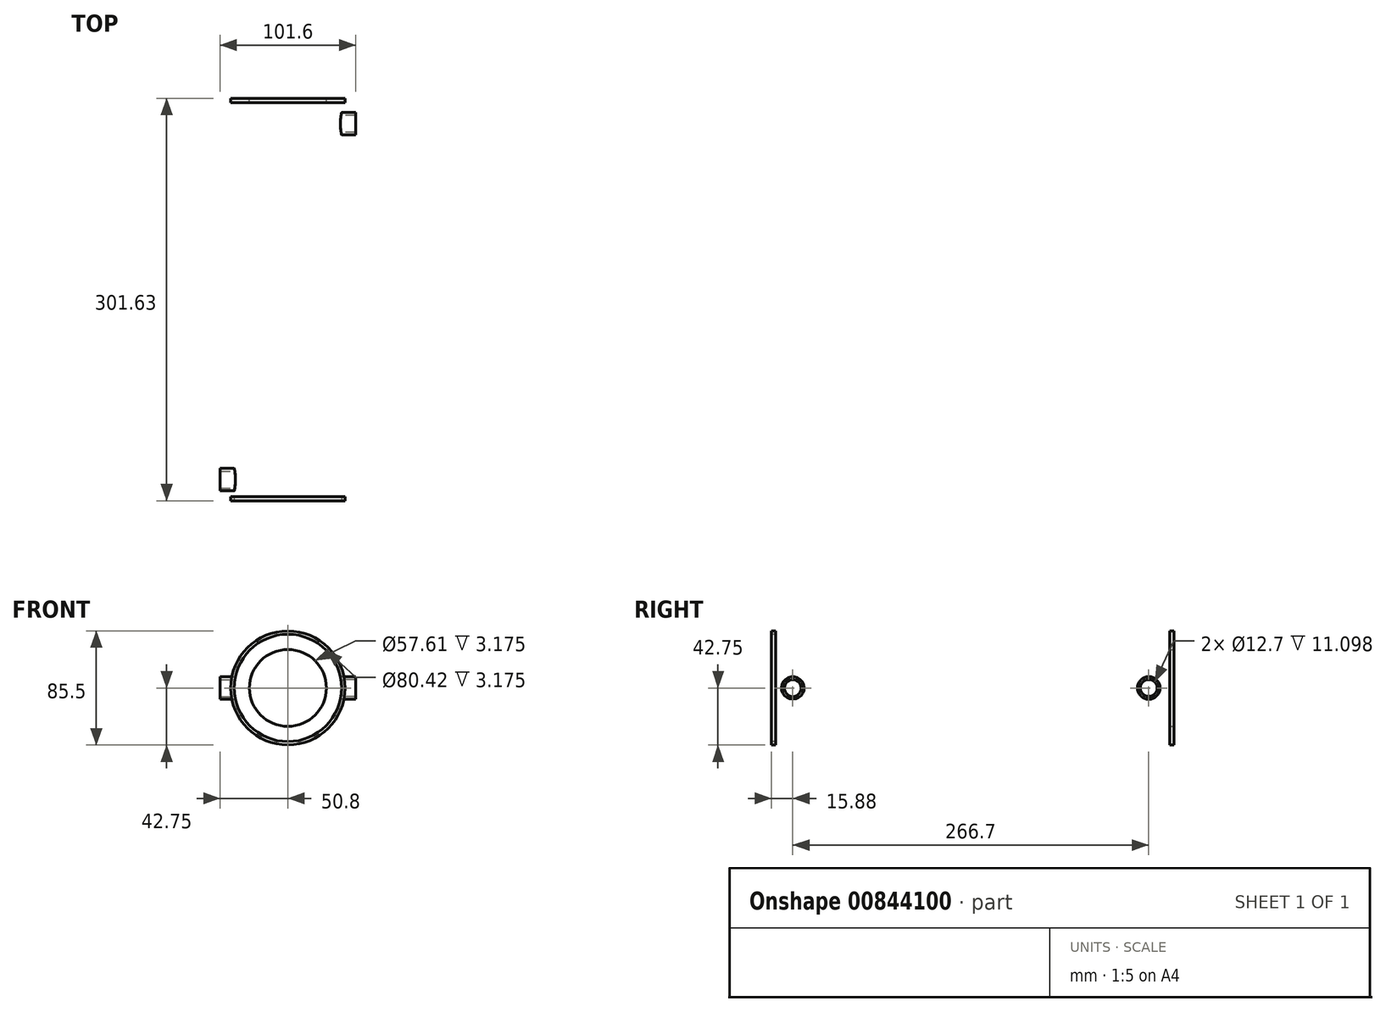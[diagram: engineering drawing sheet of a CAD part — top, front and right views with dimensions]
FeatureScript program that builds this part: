
annotation { "Feature Type Name" : "Feature", "Feature Type Description" : "" }
export const myFeature = defineFeature(function(context is Context, id is Id, definition is map)
    precondition{}
    {
        {
            var Q0;
            Q0=qCreatedBy(makeId("Front.planeOp"),FACE);
            var sketch = newSketch(context, id + "F0", { "sketchPlane" : qUnion([Q0])});
            skCircle(sketch, "E0", {"center": v(0, 0) * mm, "radius": 40.2 * mm});
            skCircle(sketch, "E1", {"center": v(0, 0) * mm, "radius": 42.75 * mm});
            skCircle(sketch, "E2", {"center": v(0, 0) * mm, "radius": 38.1 * mm});
            skCircle(sketch, "E3", {"center": v(0, 0) * mm, "radius": 28.8 * mm});
            skSolve(sketch);
        }
        {
            var Q0;
            Q0=makeQuery(id+"F0.imprint","IMPRINT",FACE,{"disambiguationData":[TD([[makeQuery(id+"F0.imprint","IMPRINT",EDGE,{"derivedFrom":sQuery(id+"F0.wireOp",EDGE,"E0")}),1.0]])]});
            extrude(context, id + "F1", {"entities" : qUnion([Q0]), "depth" : 301.62 * mm, "offsetDistance" : 25.4 * mm});
        }
        {
            var Q0;
            Q0 = qSketchRegion(id + "F0", true);
            var Q1;
            Q1=makeQuery(id+"F0.imprint","IMPRINT",FACE,{"disambiguationData":[TD([[makeQuery(id+"F0.imprint","IMPRINT",EDGE,{"derivedFrom":sQuery(id+"F0.wireOp",EDGE,"E2")}),1.0]])]});
            extrude(context, id + "F2", {"entities" : qUnion([Q0, Q1]), "operationType" : NewBodyOperationType.ADD, "depth" : 3.17 * mm, "offsetDistance" : 25.4 * mm});
        }
        {
            var Q0;
            Q0=qCreatedBy(makeId("Front.planeOp"),FACE);
            cPlane(context, id + "F3", {"entities" : qUnion([Q0]), "cplaneType" : CPlaneType.OFFSET, "offset" : 301.62 * mm, "width" : 152.4 * mm, "height" : 152.4 * mm});
        }
        {
            var Q0;
            Q0=qCreatedBy(id+"F3.planeOp",FACE);
            var sketch = newSketch(context, id + "F4", { "sketchPlane" : qUnion([Q0])});
            skCircle(sketch, "E4", {"center": v(0, 0) * mm, "radius": 42.75 * mm});
            skCircle(sketch, "E5", {"center": v(0, 0) * mm, "radius": 40.2 * mm});
            skCircle(sketch, "E6", {"center": v(0, 0) * mm, "radius": 28.8 * mm});
            skSolve(sketch);
        }
        {
            var Q0;
            Q0=makeQuery(id+"F4.imprint","IMPRINT",FACE,{"disambiguationData":[TD([[makeQuery(id+"F4.imprint","IMPRINT",EDGE,{"derivedFrom":sQuery(id+"F4.wireOp",EDGE,"E5")}),1.0]])]});
            var Q1;
            Q1=makeQuery(id+"F4.imprint","IMPRINT",FACE,{"disambiguationData":[TD([[makeQuery(id+"F4.imprint","IMPRINT",EDGE,{"derivedFrom":sQuery(id+"F4.wireOp",EDGE,"E4")}),1.0]])]});
            extrude(context, id + "F5", {"entities" : qUnion([Q0, Q1]), "operationType" : NewBodyOperationType.ADD, "oppositeDirection" : true, "depth" : 3.17 * mm, "offsetDistance" : 25.4 * mm});
        }
        {
            var Q0;
            Q0=qCreatedBy(makeId("Right.planeOp"),FACE);
            var sketch = newSketch(context, id + "F6", { "sketchPlane" : qUnion([Q0])});
            skCircle(sketch, "E7", {"center": v(-285.75, 0) * mm, "radius": 8.46 * mm});
            skCircle(sketch, "E8", {"center": v(-19.05, 0) * mm, "radius": 8.46 * mm});
            skCircle(sketch, "E9", {"center": v(-19.05, 0) * mm, "radius": 6.35 * mm});
            skCircle(sketch, "E10", {"center": v(-285.75, 0) * mm, "radius": 6.35 * mm});
            skSolve(sketch);
        }
        {
            var Q0;
            Q0=makeQuery(id+"F6.imprint","IMPRINT",FACE,{"disambiguationData":[TD([[makeQuery(id+"F6.imprint","IMPRINT",EDGE,{"derivedFrom":sQuery(id+"F6.wireOp",EDGE,"E8")}),1.0]])]});
            extrude(context, id + "F7", {"entities" : qUnion([Q0]), "depth" : 50.8 * mm, "offsetDistance" : 25.4 * mm});
        }
        {
            var Q0;
            Q0=makeQuery(id+"F6.imprint","IMPRINT",FACE,{"disambiguationData":[TD([[makeQuery(id+"F6.imprint","IMPRINT",EDGE,{"derivedFrom":sQuery(id+"F6.wireOp",EDGE,"E7")}),1.0]])]});
            extrude(context, id + "F8", {"entities" : qUnion([Q0]), "oppositeDirection" : true, "depth" : 50.8 * mm, "offsetDistance" : 25.4 * mm});
        }
        {
            var Q0;
            Q0=sQuery(id+"F6.wireOp",VERTEX,"E8.center");
            var Q1;
            Q1=makeQuery(id+"F1.opExtrude","SWEPT_BODY",BODY,{"disambiguationData":[OSD([sQuery(id+"F0.wireOp",EDGE,"E0"),sQuery(id+"F0.wireOp",EDGE,"E2")])]});
            hole(context, id + "F9", {"style" : HoleStyle.SIMPLE, "endStyle" : HoleEndStyle.THROUGH, "oppositeDirection" : true, "holeDiameter" : 12.7 * mm, "majorDiameter" : 6.35 * mm, "isTappedThrough" : true, "tappedDepth" : 12.7 * mm, "tapClearance" : 3, "locations" : qUnion([Q0]), "scope" : qUnion([Q1])});
        }
        {
            var Q0;
            Q0=sQuery(id+"F6.wireOp",VERTEX,"E7.center");
            var Q1;
            Q1=makeQuery(id+"F1.opExtrude","SWEPT_BODY",BODY,{"disambiguationData":[OSD([sQuery(id+"F0.wireOp",EDGE,"E0"),sQuery(id+"F0.wireOp",EDGE,"E2")])]});
            hole(context, id + "F10", {"style" : HoleStyle.SIMPLE, "endStyle" : HoleEndStyle.THROUGH, "holeDiameter" : 12.7 * mm, "majorDiameter" : 6.35 * mm, "isTappedThrough" : true, "tappedDepth" : 12.7 * mm, "tapClearance" : 3, "locations" : qUnion([Q0]), "scope" : qUnion([Q1])});
        }
        {
            var Q0;
            Q0=makeQuery(id+"F4.imprint","IMPRINT",FACE,{"disambiguationData":[TD([[makeQuery(id+"F4.imprint","IMPRINT",EDGE,{"derivedFrom":sQuery(id+"F4.wireOp",EDGE,"E5")}),1.0]])]});
            var Q1;
            Q1=makeQuery(id+"F4.imprint","IMPRINT",FACE,{"disambiguationData":[TD([[makeQuery(id+"F4.imprint","IMPRINT",EDGE,{"derivedFrom":sQuery(id+"F4.wireOp",EDGE,"E6")}),1.0]])]});
            var Q2;
            Q2=sQuery(id+"F4.wireOp",EDGE,"E5");
            extrude(context, id + "F11", {"entities" : qUnion([Q0, Q1]), "operationType" : NewBodyOperationType.REMOVE, "surfaceEntities" : qUnion([Q2]), "oppositeDirection" : true, "depth" : 298.45 * mm, "offsetDistance" : 25.4 * mm});
        }
    });
